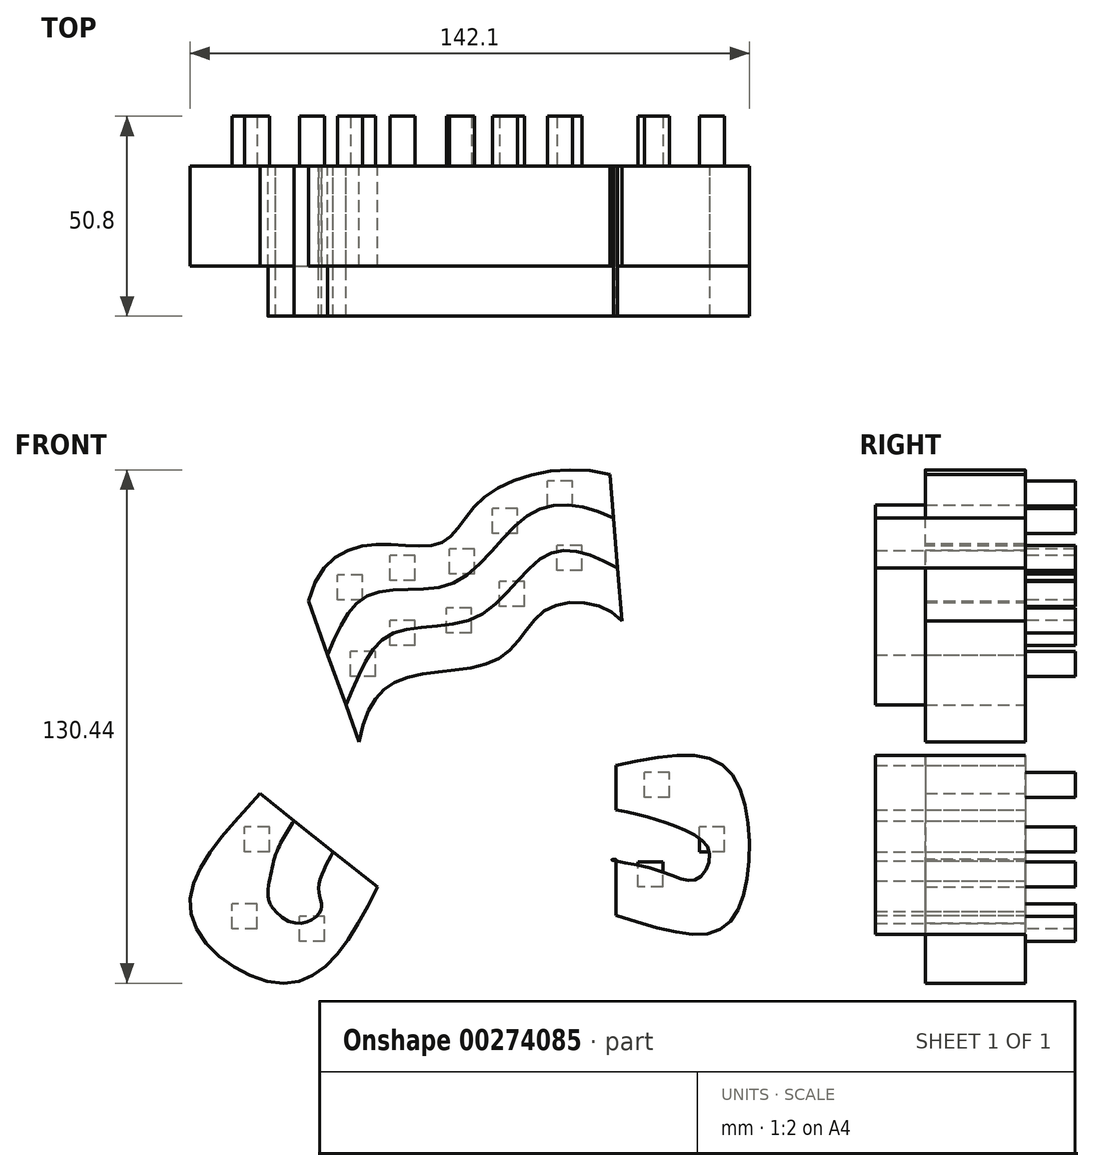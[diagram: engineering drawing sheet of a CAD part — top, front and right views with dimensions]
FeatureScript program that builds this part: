
annotation { "Feature Type Name" : "Feature", "Feature Type Description" : "" }
export const myFeature = defineFeature(function(context is Context, id is Id, definition is map)
    precondition{}
    {
        {
            var Q0;
            Q0=qCreatedBy(makeId("Front.planeOp"),FACE);
            var sketch = newSketch(context, id + "F0", { "sketchPlane" : qUnion([Q0])});
            skLineSegment(sketch, "E0", {"start": v(-36.25, -7.17) * mm, "end": v(-6.46, -30.91) * mm});
            skFitSpline(sketch, "E1", {"points": [v(-36.25, -7.17) * mm, v(-53.83, -37.42) * mm, v(-29.13, -55.3) * mm, v(-6.46, -30.91) * mm], "startDerivative": vector(-70.76, -79.8) * mm, "endDerivative": vector(54.49, 111.1) * mm});
            skFitSpline(sketch, "E2", {"points": [v(-23.98, 41.77) * mm, v(-7.34, 56.11) * mm, v(9.99, 56.6) * mm, v(20.5, 67.95) * mm, v(52.6, 73.94) * mm], "startDerivative": vector(30.08, 121.18) * mm, "endDerivative": vector(112.99, -29.07) * mm});
            skLineSegment(sketch, "E3", {"start": v(52.6, 73.94) * mm, "end": v(55.73, 35.97) * mm});
            skFitSpline(sketch, "E4", {"points": [v(-11.07, 5.92) * mm, v(0, 22) * mm, v(24.74, 27.28) * mm, v(37.27, 40) * mm, v(55.73, 36.67) * mm], "startDerivative": vector(19.92, 108.13) * mm, "endDerivative": vector(48.44, -58.3) * mm});
            skLineSegment(sketch, "E5", {"start": v(-23.98, 41.77) * mm, "end": v(-11.07, 5.92) * mm});
            skLineSegment(sketch, "E6", {"start": v(54.13, 0) * mm, "end": v(54.13, -38.1) * mm});
            skFitSpline(sketch, "E7", {"points": [v(54.13, 0) * mm, v(81.4, 0) * mm, v(88.01, -23.23) * mm, v(80.7, -41.68) * mm, v(54.13, -38.1) * mm], "startDerivative": vector(129.75, 26.06) * mm, "endDerivative": vector(-126.97, 39.06) * mm});
            skFitSpline(sketch, "E8", {"points": [v(-34.95, -36.36) * mm, v(-32.25, -22.65) * mm, v(-27.62, -14.05) * mm], "startDerivative": vector(3.93, 24.07) * mm, "endDerivative": vector(10.96, 17.23) * mm});
            skArc(sketch, "E9.filletArc", {"start": v(-34.2, -31.46) * mm, "mid": v(-33.94, -34.48) * mm, "end": v(-32.3, -37.04) * mm});
            skPoint(sketch, "E10.2.internal.snap0", {"position": v(-21.35, -19.04) * mm});
            skFitSpline(sketch, "E10", {"points": [v(-32.3, -37.04) * mm, v(-20.93, -37.04) * mm, v(-21.35, -31.46) * mm, v(-17.69, -21.96) * mm], "startDerivative": vector(37.87, -43.37) * mm, "endDerivative": vector(12.85, 23.54) * mm});
            skFitSpline(sketch, "E11", {"points": [v(-19.05, 28.07) * mm, v(-8.08, 43.5) * mm, v(13.12, 46.46) * mm, v(32.85, 64.16) * mm, v(53.51, 62.86) * mm], "startDerivative": vector(37.58, 92.32) * mm, "endDerivative": vector(89.2, -41.4) * mm});
            skFitSpline(sketch, "E12", {"points": [v(-14.48, 15.37) * mm, v(-3.29, 33.18) * mm, v(19.02, 37.8) * mm, v(36.9, 53.65) * mm, v(54.56, 50.16) * mm], "startDerivative": vector(41.67, 89.02) * mm, "endDerivative": vector(81.87, -44.15) * mm});
            skFitSpline(sketch, "E13", {"points": [v(54.13, -11.27) * mm, v(68.57, -15.23) * mm, v(77.83, -21.75) * mm, v(74.75, -28.95) * mm, v(64.37, -26.55) * mm, v(53.13, -23.97) * mm, v(54.13, -23.97) * mm], "startDerivative": vector(77.13, -13.17) * mm, "endDerivative": vector(-14.41, -1.68) * mm});
            skSolve(sketch);
        }
        {
            var Q0;
            Q0=qCreatedBy(makeId("Front.planeOp"),FACE);
            var sketch = newSketch(context, id + "F1", { "sketchPlane" : qUnion([Q0])});
            skLineSegment(sketch, "E14.bottom", {"start": v(-37.05, -41.52) * mm, "end": v(-43.4, -41.52) * mm});
            skLineSegment(sketch, "E14.top", {"start": v(-37.05, -35.17) * mm, "end": v(-43.4, -35.17) * mm});
            skLineSegment(sketch, "E14.left", {"start": v(-37.05, -41.52) * mm, "end": v(-37.05, -35.17) * mm});
            skLineSegment(sketch, "E14.right", {"start": v(-43.4, -41.52) * mm, "end": v(-43.4, -35.17) * mm});
            skPoint(sketch, "E14.middle", {"position": v(-40.23, -38.35) * mm});
            skLineSegment(sketch, "E15.bottom", {"start": v(-33.88, -21.98) * mm, "end": v(-40.23, -21.98) * mm});
            skLineSegment(sketch, "E15.top", {"start": v(-33.88, -15.63) * mm, "end": v(-40.23, -15.63) * mm});
            skLineSegment(sketch, "E15.left", {"start": v(-33.88, -21.98) * mm, "end": v(-33.88, -15.63) * mm});
            skLineSegment(sketch, "E15.right", {"start": v(-40.23, -21.98) * mm, "end": v(-40.23, -15.63) * mm});
            skPoint(sketch, "E15.middle", {"position": v(-37.05, -18.8) * mm});
            skLineSegment(sketch, "E16.bottom", {"start": v(-19.86, -44.7) * mm, "end": v(-26.2, -44.7) * mm});
            skLineSegment(sketch, "E16.top", {"start": v(-19.86, -38.35) * mm, "end": v(-26.2, -38.35) * mm});
            skLineSegment(sketch, "E16.left", {"start": v(-19.86, -44.7) * mm, "end": v(-19.86, -38.35) * mm});
            skLineSegment(sketch, "E16.right", {"start": v(-26.2, -44.7) * mm, "end": v(-26.2, -38.35) * mm});
            skPoint(sketch, "E16.middle", {"position": v(-23.03, -41.52) * mm});
            skLineSegment(sketch, "E17.bottom", {"start": v(-6.86, 22.63) * mm, "end": v(-13.21, 22.63) * mm});
            skLineSegment(sketch, "E17.top", {"start": v(-6.86, 28.98) * mm, "end": v(-13.21, 28.98) * mm});
            skLineSegment(sketch, "E17.left", {"start": v(-6.86, 22.63) * mm, "end": v(-6.86, 28.98) * mm});
            skLineSegment(sketch, "E17.right", {"start": v(-13.21, 22.63) * mm, "end": v(-13.21, 28.98) * mm});
            skPoint(sketch, "E17.middle", {"position": v(-10.04, 25.8) * mm});
            skLineSegment(sketch, "E18.bottom", {"start": v(-10.18, 41.99) * mm, "end": v(-16.53, 41.99) * mm});
            skLineSegment(sketch, "E18.top", {"start": v(-10.18, 48.34) * mm, "end": v(-16.53, 48.34) * mm});
            skLineSegment(sketch, "E18.left", {"start": v(-10.18, 41.99) * mm, "end": v(-10.18, 48.34) * mm});
            skLineSegment(sketch, "E18.right", {"start": v(-16.53, 41.99) * mm, "end": v(-16.53, 48.34) * mm});
            skPoint(sketch, "E18.middle", {"position": v(-13.36, 45.16) * mm});
            skLineSegment(sketch, "E19.bottom", {"start": v(3.18, 30.52) * mm, "end": v(-3.17, 30.52) * mm});
            skLineSegment(sketch, "E19.top", {"start": v(3.18, 36.87) * mm, "end": v(-3.18, 36.87) * mm});
            skLineSegment(sketch, "E19.left", {"start": v(3.18, 30.52) * mm, "end": v(3.17, 36.87) * mm});
            skLineSegment(sketch, "E19.right", {"start": v(-3.18, 30.52) * mm, "end": v(-3.18, 36.87) * mm});
            skPoint(sketch, "E19.middle", {"position": v(0, 33.7) * mm});
            skLineSegment(sketch, "E20.bottom", {"start": v(3.17, 46.96) * mm, "end": v(-3.18, 46.96) * mm});
            skLineSegment(sketch, "E20.top", {"start": v(3.17, 53.31) * mm, "end": v(-3.18, 53.31) * mm});
            skLineSegment(sketch, "E20.left", {"start": v(3.18, 46.96) * mm, "end": v(3.18, 53.31) * mm});
            skLineSegment(sketch, "E20.right", {"start": v(-3.17, 46.96) * mm, "end": v(-3.18, 53.31) * mm});
            skPoint(sketch, "E20.middle", {"position": v(0, 50.14) * mm});
            skLineSegment(sketch, "E21.bottom", {"start": v(17.47, 33.7) * mm, "end": v(11.12, 33.7) * mm});
            skLineSegment(sketch, "E21.top", {"start": v(17.47, 40.04) * mm, "end": v(11.12, 40.04) * mm});
            skLineSegment(sketch, "E21.left", {"start": v(17.47, 33.7) * mm, "end": v(17.47, 40.04) * mm});
            skLineSegment(sketch, "E21.right", {"start": v(11.12, 33.7) * mm, "end": v(11.12, 40.04) * mm});
            skPoint(sketch, "E21.middle", {"position": v(14.3, 36.87) * mm});
            skLineSegment(sketch, "E22.bottom", {"start": v(18.23, 48.62) * mm, "end": v(11.88, 48.62) * mm});
            skLineSegment(sketch, "E22.top", {"start": v(18.23, 54.97) * mm, "end": v(11.88, 54.97) * mm});
            skLineSegment(sketch, "E22.left", {"start": v(18.23, 48.62) * mm, "end": v(18.23, 54.97) * mm});
            skLineSegment(sketch, "E22.right", {"start": v(11.88, 48.62) * mm, "end": v(11.88, 54.97) * mm});
            skPoint(sketch, "E22.middle", {"position": v(15.06, 51.8) * mm});
            skLineSegment(sketch, "E23.bottom", {"start": v(29.09, 58.95) * mm, "end": v(22.74, 58.95) * mm});
            skLineSegment(sketch, "E23.top", {"start": v(29.09, 65.3) * mm, "end": v(22.74, 65.3) * mm});
            skLineSegment(sketch, "E23.left", {"start": v(29.09, 58.95) * mm, "end": v(29.09, 65.3) * mm});
            skLineSegment(sketch, "E23.right", {"start": v(22.74, 58.95) * mm, "end": v(22.74, 65.3) * mm});
            skPoint(sketch, "E23.middle", {"position": v(25.91, 62.12) * mm});
            skLineSegment(sketch, "E24.bottom", {"start": v(30.93, 40.33) * mm, "end": v(24.58, 40.33) * mm});
            skLineSegment(sketch, "E24.top", {"start": v(30.93, 46.68) * mm, "end": v(24.58, 46.68) * mm});
            skLineSegment(sketch, "E24.left", {"start": v(30.93, 40.33) * mm, "end": v(30.93, 46.68) * mm});
            skLineSegment(sketch, "E24.right", {"start": v(24.58, 40.33) * mm, "end": v(24.58, 46.68) * mm});
            skPoint(sketch, "E24.middle", {"position": v(27.76, 43.5) * mm});
            skLineSegment(sketch, "E25.bottom", {"start": v(45.5, 49.54) * mm, "end": v(39.14, 49.54) * mm});
            skLineSegment(sketch, "E25.top", {"start": v(45.5, 55.9) * mm, "end": v(39.14, 55.9) * mm});
            skLineSegment(sketch, "E25.left", {"start": v(45.5, 49.54) * mm, "end": v(45.5, 55.9) * mm});
            skLineSegment(sketch, "E25.right", {"start": v(39.14, 49.54) * mm, "end": v(39.14, 55.9) * mm});
            skPoint(sketch, "E25.middle", {"position": v(42.32, 52.72) * mm});
            skLineSegment(sketch, "E26.bottom", {"start": v(43.1, 65.95) * mm, "end": v(36.75, 65.95) * mm});
            skLineSegment(sketch, "E26.top", {"start": v(43.1, 72.3) * mm, "end": v(36.75, 72.3) * mm});
            skLineSegment(sketch, "E26.left", {"start": v(43.1, 65.95) * mm, "end": v(43.1, 72.3) * mm});
            skLineSegment(sketch, "E26.right", {"start": v(36.75, 65.95) * mm, "end": v(36.75, 72.3) * mm});
            skPoint(sketch, "E26.middle", {"position": v(39.92, 69.13) * mm});
            skLineSegment(sketch, "E27.bottom", {"start": v(67.8, -8.16) * mm, "end": v(61.45, -8.16) * mm});
            skLineSegment(sketch, "E27.top", {"start": v(67.8, -1.8) * mm, "end": v(61.45, -1.8) * mm});
            skLineSegment(sketch, "E27.left", {"start": v(67.8, -8.16) * mm, "end": v(67.8, -1.8) * mm});
            skLineSegment(sketch, "E27.right", {"start": v(61.45, -8.16) * mm, "end": v(61.45, -1.8) * mm});
            skPoint(sketch, "E27.middle", {"position": v(64.63, -4.98) * mm});
            skLineSegment(sketch, "E28.bottom", {"start": v(81.75, -21.98) * mm, "end": v(75.4, -21.98) * mm});
            skLineSegment(sketch, "E28.top", {"start": v(81.75, -15.63) * mm, "end": v(75.4, -15.63) * mm});
            skLineSegment(sketch, "E28.left", {"start": v(81.75, -21.98) * mm, "end": v(81.75, -15.63) * mm});
            skLineSegment(sketch, "E28.right", {"start": v(75.4, -21.98) * mm, "end": v(75.4, -15.63) * mm});
            skPoint(sketch, "E28.middle", {"position": v(78.57, -18.8) * mm});
            skLineSegment(sketch, "E29.bottom", {"start": v(66.08, -30.83) * mm, "end": v(59.73, -30.83) * mm});
            skLineSegment(sketch, "E29.top", {"start": v(66.08, -24.48) * mm, "end": v(59.73, -24.48) * mm});
            skLineSegment(sketch, "E29.left", {"start": v(66.08, -30.83) * mm, "end": v(66.08, -24.48) * mm});
            skLineSegment(sketch, "E29.right", {"start": v(59.73, -30.83) * mm, "end": v(59.73, -24.48) * mm});
            skPoint(sketch, "E29.middle", {"position": v(62.9, -27.65) * mm});
            skPoint(sketch, "E30", {"position": v(14.3, 33.7) * mm});
            skSolve(sketch);
        }
        {
            var Q0;
            Q0 = qSketchRegion(id + "F1", true);
            var Q1;
            {var subQ0=sQuery(id+"F0.wireOp",EDGE,"E8");Q1=makeQuery(id+"F0.imprint","IMPRINT",FACE,{"disambiguationData":[TD([[makeQuery(id+"F0.imprint","IMPRINT",EDGE,{"derivedFrom":subQ0}),-1.0]])]});}
            var Q2;
            {var subQ0=sQuery(id+"F0.wireOp",EDGE,"E11");Q2=makeQuery(id+"F0.imprint","IMPRINT",FACE,{"disambiguationData":[TD([[makeQuery(id+"F0.imprint","IMPRINT",EDGE,{"derivedFrom":subQ0}),-1.0]])]});}
            var Q3;
            {var subQ0=sQuery(id+"F0.wireOp",EDGE,"E13");var subQ1=sQuery(id+"F0.wireOp",EDGE,"E6");var subQ2=makeQuery(id+"F0.imprint","INTERSECT",VERTEX,{"disambiguationData":[OD(0.0)],"derivedFrom":[subQ1,subQ0]});Q3=makeQuery(id+"F0.imprint","IMPRINT",FACE,{"disambiguationData":[TD([[makeQuery(id+"F0.imprint","IMPRINT",EDGE,{"disambiguationData":[TD([[subQ2,-1.0]])],"derivedFrom":subQ1}),1.0]])]});}
            extrude(context, id + "F2", {"entities" : qUnion([Q0, Q1, Q2, Q3]), "depth" : 38.1 * mm});
        }
        {
            var Q0;
            {var subQ1=sQuery(id+"F0.wireOp",EDGE,"E1");Q0=makeQuery(id+"F0.imprint","IMPRINT",FACE,{"disambiguationData":[TD([[makeQuery(id+"F0.imprint","IMPRINT",EDGE,{"derivedFrom":subQ1}),1.0]])]});}
            var Q1;
            {var subQ0=sQuery(id+"F0.wireOp",EDGE,"E2");Q1=makeQuery(id+"F0.imprint","IMPRINT",FACE,{"disambiguationData":[TD([[makeQuery(id+"F0.imprint","IMPRINT",EDGE,{"derivedFrom":subQ0}),-1.0]])]});}
            var Q2;
            {var subQ0=sQuery(id+"F0.wireOp",EDGE,"E12");Q2=makeQuery(id+"F0.imprint","IMPRINT",FACE,{"disambiguationData":[TD([[makeQuery(id+"F0.imprint","IMPRINT",EDGE,{"derivedFrom":subQ0}),-1.0]])]});}
            var Q3;
            {var subQ0=sQuery(id+"F0.wireOp",EDGE,"E7");Q3=makeQuery(id+"F0.imprint","IMPRINT",FACE,{"disambiguationData":[TD([[makeQuery(id+"F0.imprint","IMPRINT",EDGE,{"derivedFrom":subQ0}),-1.0]])]});}
            var Q4;
            {var subQ0=sQuery(id+"F0.wireOp",EDGE,"E13");var subQ1=sQuery(id+"F0.wireOp",EDGE,"E6");var subQ2=makeQuery(id+"F0.imprint","INTERSECT",VERTEX,{"disambiguationData":[OD(1.0)],"derivedFrom":[subQ1,subQ0]});Q4=makeQuery(id+"F0.imprint","IMPRINT",FACE,{"disambiguationData":[TD([[makeQuery(id+"F0.imprint","IMPRINT",EDGE,{"disambiguationData":[TD([[subQ2,1.0]])],"derivedFrom":subQ1}),-1.0]])]});}
            var Q5;
            {var subQ0=sQuery(id+"F0.wireOp",EDGE,"E13");var subQ1=sQuery(id+"F0.wireOp",EDGE,"E6");var subQ2=makeQuery(id+"F0.imprint","INTERSECT",VERTEX,{"disambiguationData":[OD(1.0)],"derivedFrom":[subQ1,subQ0]});Q5=makeQuery(id+"F0.imprint","IMPRINT",FACE,{"disambiguationData":[TD([[makeQuery(id+"F0.imprint","IMPRINT",EDGE,{"disambiguationData":[TD([[subQ2,1.0]])],"derivedFrom":subQ1}),1.0]])]});}
            extrude(context, id + "F3", {"entities" : qUnion([Q0, Q1, Q2, Q3, Q4, Q5]), "depth" : 25.4 * mm});
        }
        {
            var Q0;
            Q0=makeQuery(id+"F2.opExtrude","SWEPT_BODY",BODY,{"disambiguationData":[OSD([sQuery(id+"F1.wireOp",EDGE,"E14.bottom"),sQuery(id+"F1.wireOp",EDGE,"E14.top"),sQuery(id+"F1.wireOp",EDGE,"E14.left"),sQuery(id+"F1.wireOp",EDGE,"E14.right")])]});
            var Q1;
            Q1=makeQuery(id+"F2.opExtrude","SWEPT_BODY",BODY,{"disambiguationData":[OSD([sQuery(id+"F1.wireOp",EDGE,"E15.bottom"),sQuery(id+"F1.wireOp",EDGE,"E15.top"),sQuery(id+"F1.wireOp",EDGE,"E15.left"),sQuery(id+"F1.wireOp",EDGE,"E15.right")])]});
            var Q2;
            Q2=makeQuery(id+"F2.opExtrude","SWEPT_BODY",BODY,{"disambiguationData":[OSD([sQuery(id+"F1.wireOp",EDGE,"E16.bottom"),sQuery(id+"F1.wireOp",EDGE,"E16.top"),sQuery(id+"F1.wireOp",EDGE,"E16.left"),sQuery(id+"F1.wireOp",EDGE,"E16.right")])]});
            var Q3;
            Q3=makeQuery(id+"F2.opExtrude","SWEPT_BODY",BODY,{"disambiguationData":[OSD([sQuery(id+"F1.wireOp",EDGE,"E17.bottom"),sQuery(id+"F1.wireOp",EDGE,"E17.top"),sQuery(id+"F1.wireOp",EDGE,"E17.left"),sQuery(id+"F1.wireOp",EDGE,"E17.right")])]});
            var Q4;
            Q4=makeQuery(id+"F2.opExtrude","SWEPT_BODY",BODY,{"disambiguationData":[OSD([sQuery(id+"F1.wireOp",EDGE,"E18.bottom"),sQuery(id+"F1.wireOp",EDGE,"E18.top"),sQuery(id+"F1.wireOp",EDGE,"E18.left"),sQuery(id+"F1.wireOp",EDGE,"E18.right")])]});
            var Q5;
            Q5=makeQuery(id+"F2.opExtrude","SWEPT_BODY",BODY,{"disambiguationData":[OSD([sQuery(id+"F1.wireOp",EDGE,"E19.bottom"),sQuery(id+"F1.wireOp",EDGE,"E19.top"),sQuery(id+"F1.wireOp",EDGE,"E19.left"),sQuery(id+"F1.wireOp",EDGE,"E19.right")])]});
            var Q6;
            Q6=makeQuery(id+"F2.opExtrude","SWEPT_BODY",BODY,{"disambiguationData":[OSD([sQuery(id+"F1.wireOp",EDGE,"E20.bottom"),sQuery(id+"F1.wireOp",EDGE,"E20.top"),sQuery(id+"F1.wireOp",EDGE,"E20.left"),sQuery(id+"F1.wireOp",EDGE,"E20.right")])]});
            var Q7;
            Q7=makeQuery(id+"F2.opExtrude","SWEPT_BODY",BODY,{"disambiguationData":[OSD([sQuery(id+"F1.wireOp",EDGE,"E21.bottom"),sQuery(id+"F1.wireOp",EDGE,"E21.top"),sQuery(id+"F1.wireOp",EDGE,"E21.left"),sQuery(id+"F1.wireOp",EDGE,"E21.right")])]});
            var Q8;
            Q8=makeQuery(id+"F2.opExtrude","SWEPT_BODY",BODY,{"disambiguationData":[OSD([sQuery(id+"F1.wireOp",EDGE,"E22.bottom"),sQuery(id+"F1.wireOp",EDGE,"E22.top"),sQuery(id+"F1.wireOp",EDGE,"E22.left"),sQuery(id+"F1.wireOp",EDGE,"E22.right")])]});
            var Q9;
            Q9=makeQuery(id+"F2.opExtrude","SWEPT_BODY",BODY,{"disambiguationData":[OSD([sQuery(id+"F1.wireOp",EDGE,"E23.bottom"),sQuery(id+"F1.wireOp",EDGE,"E23.top"),sQuery(id+"F1.wireOp",EDGE,"E23.left"),sQuery(id+"F1.wireOp",EDGE,"E23.right")])]});
            var Q10;
            Q10=makeQuery(id+"F2.opExtrude","SWEPT_BODY",BODY,{"disambiguationData":[OSD([sQuery(id+"F1.wireOp",EDGE,"E24.bottom"),sQuery(id+"F1.wireOp",EDGE,"E24.top"),sQuery(id+"F1.wireOp",EDGE,"E24.left"),sQuery(id+"F1.wireOp",EDGE,"E24.right")])]});
            var Q11;
            Q11=makeQuery(id+"F2.opExtrude","SWEPT_BODY",BODY,{"disambiguationData":[OSD([sQuery(id+"F1.wireOp",EDGE,"E25.bottom"),sQuery(id+"F1.wireOp",EDGE,"E25.top"),sQuery(id+"F1.wireOp",EDGE,"E25.left"),sQuery(id+"F1.wireOp",EDGE,"E25.right")])]});
            var Q12;
            Q12=makeQuery(id+"F2.opExtrude","SWEPT_BODY",BODY,{"disambiguationData":[OSD([sQuery(id+"F1.wireOp",EDGE,"E26.bottom"),sQuery(id+"F1.wireOp",EDGE,"E26.top"),sQuery(id+"F1.wireOp",EDGE,"E26.left"),sQuery(id+"F1.wireOp",EDGE,"E26.right")])]});
            var Q13;
            Q13=makeQuery(id+"F2.opExtrude","SWEPT_BODY",BODY,{"disambiguationData":[OSD([sQuery(id+"F1.wireOp",EDGE,"E27.bottom"),sQuery(id+"F1.wireOp",EDGE,"E27.top"),sQuery(id+"F1.wireOp",EDGE,"E27.left"),sQuery(id+"F1.wireOp",EDGE,"E27.right")])]});
            var Q14;
            Q14=makeQuery(id+"F2.opExtrude","SWEPT_BODY",BODY,{"disambiguationData":[OSD([sQuery(id+"F1.wireOp",EDGE,"E28.bottom"),sQuery(id+"F1.wireOp",EDGE,"E28.top"),sQuery(id+"F1.wireOp",EDGE,"E28.left"),sQuery(id+"F1.wireOp",EDGE,"E28.right")])]});
            var Q15;
            Q15=makeQuery(id+"F2.opExtrude","SWEPT_BODY",BODY,{"disambiguationData":[OSD([sQuery(id+"F1.wireOp",EDGE,"E29.bottom"),sQuery(id+"F1.wireOp",EDGE,"E29.top"),sQuery(id+"F1.wireOp",EDGE,"E29.left"),sQuery(id+"F1.wireOp",EDGE,"E29.right")])]});
            deleteBodies(context, id + "F4", {"entities" : qUnion([Q0, Q1, Q2, Q3, Q4, Q5, Q6, Q7, Q8, Q9, Q10, Q11, Q12, Q13, Q14, Q15])});
        }
        {
            var Q0;
            Q0 = qSketchRegion(id + "F1", true);
            extrude(context, id + "F5", {"entities" : qUnion([Q0]), "oppositeDirection" : true, "depth" : 12.7 * mm});
        }
    });
